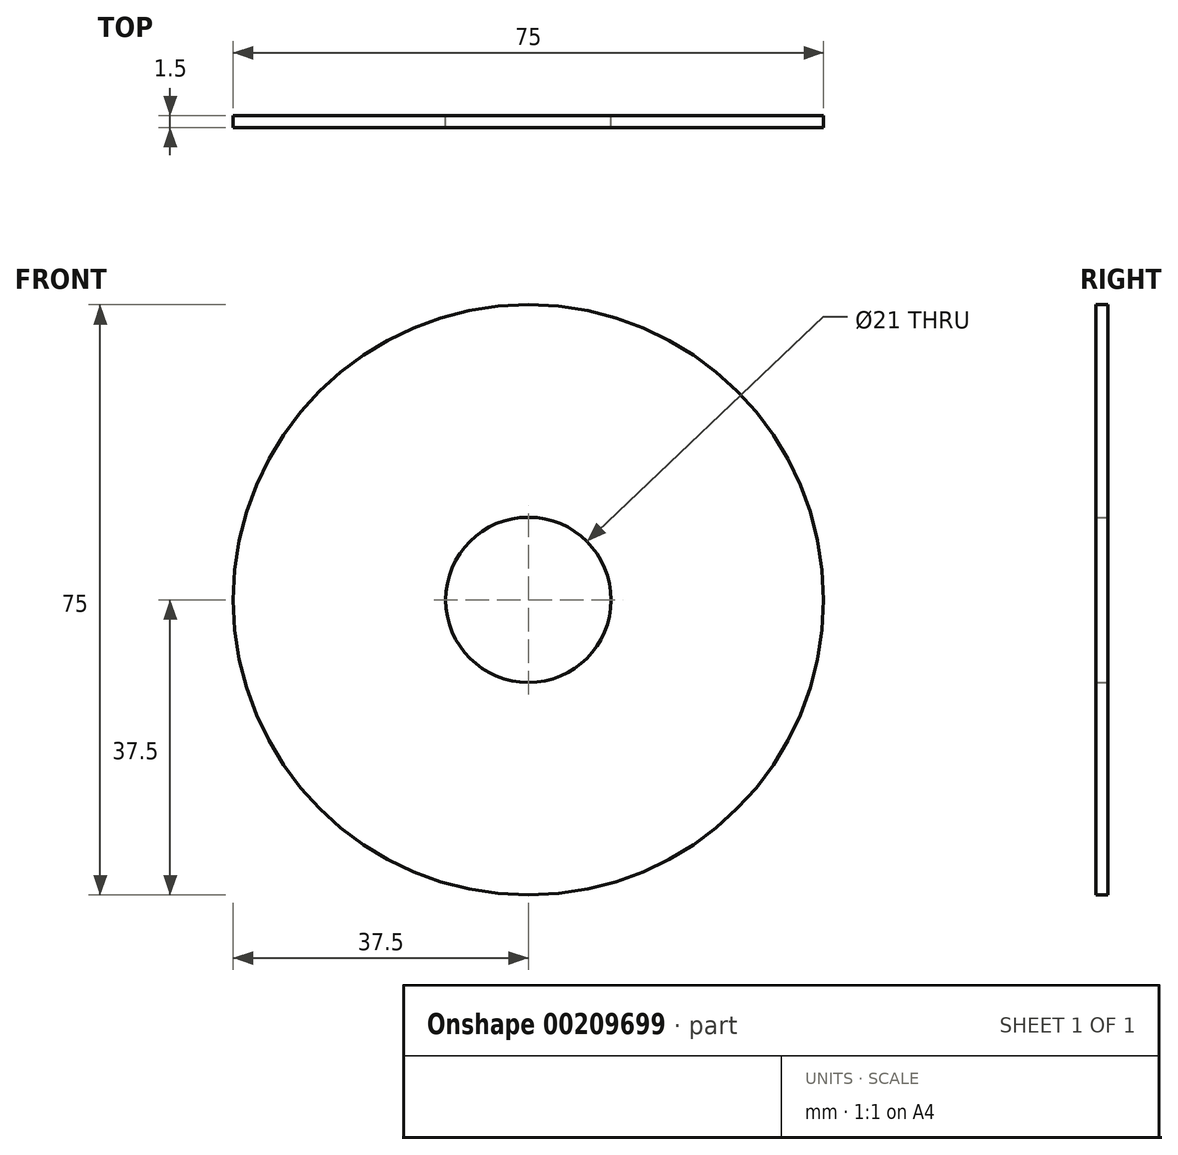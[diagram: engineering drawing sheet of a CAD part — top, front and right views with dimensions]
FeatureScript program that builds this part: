
annotation { "Feature Type Name" : "Feature", "Feature Type Description" : "" }
export const myFeature = defineFeature(function(context is Context, id is Id, definition is map)
    precondition{}
    {
        {
            var Q0;
            Q0=qCreatedBy(makeId("Front.planeOp"),FACE);
            var sketch = newSketch(context, id + "F0", { "sketchPlane" : qUnion([Q0])});
            skCircle(sketch, "E0", {"center": v(0, 0) * mm, "radius": 37.5 * mm});
            skCircle(sketch, "E1", {"center": v(0, 0) * mm, "radius": 10.5 * mm});
            skSolve(sketch);
        }
        {
            var Q0;
            Q0=makeQuery(id+"F0.imprint","IMPRINT",FACE,{"disambiguationData":[TD([[makeQuery(id+"F0.imprint","IMPRINT",EDGE,{"derivedFrom":sQuery(id+"F0.wireOp",EDGE,"E0")}),1.0]])]});
            extrude(context, id + "F1", {"entities" : qUnion([Q0]), "depth" : 1.5 * mm});
        }
    });
